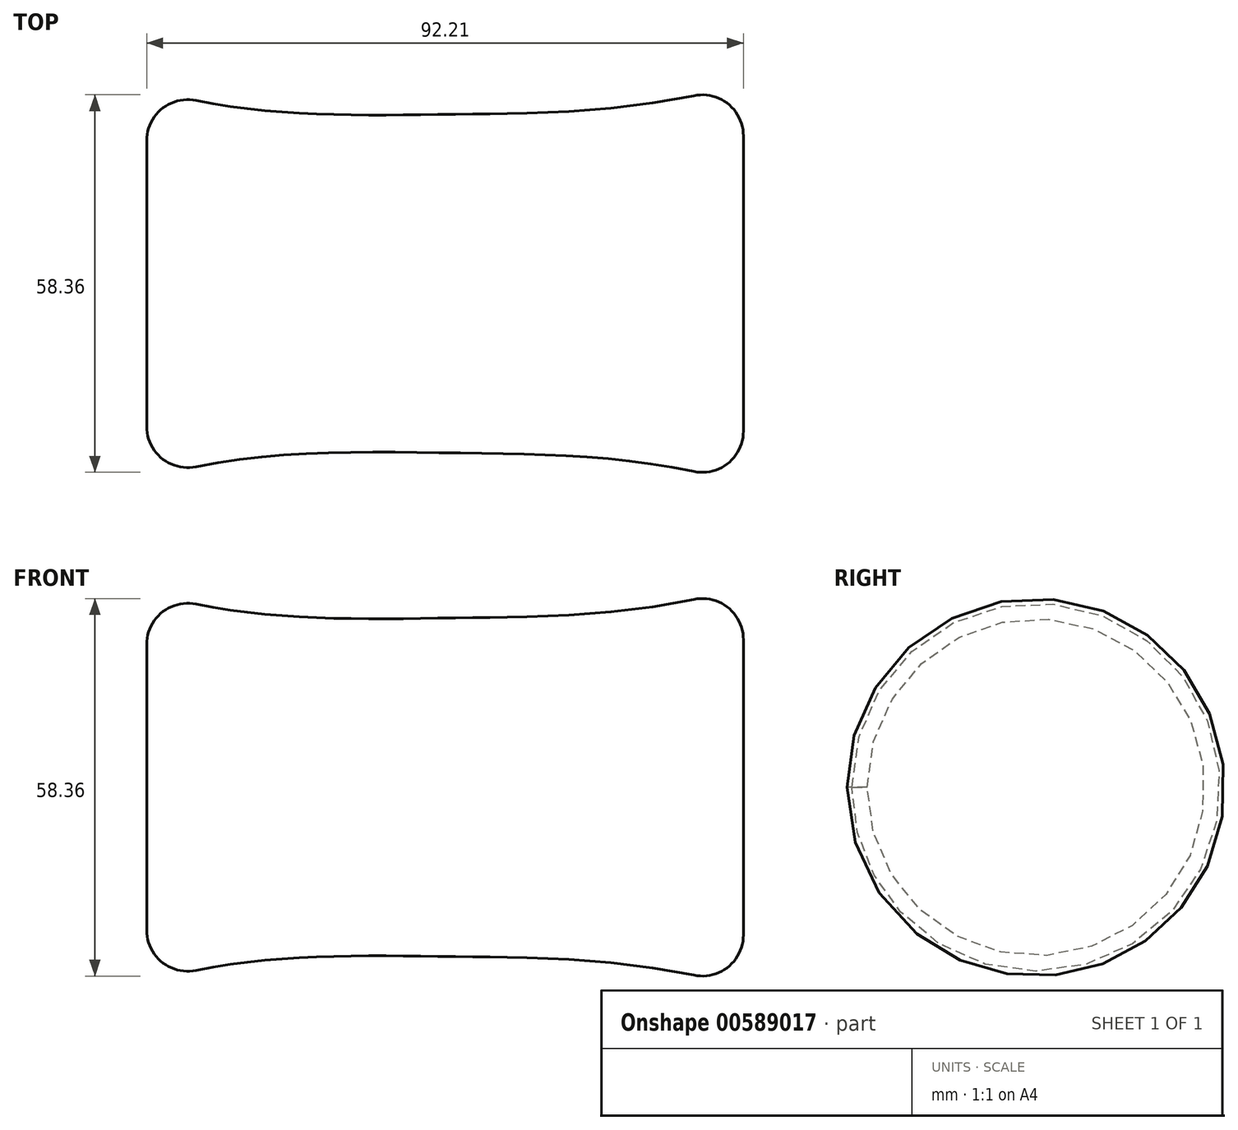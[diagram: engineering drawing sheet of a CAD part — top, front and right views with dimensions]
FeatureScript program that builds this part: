
annotation { "Feature Type Name" : "Feature", "Feature Type Description" : "" }
export const myFeature = defineFeature(function(context is Context, id is Id, definition is map)
    precondition{}
    {
        {
            var Q0;
            Q0=qCreatedBy(makeId("Top.planeOp"),FACE);
            var sketch = newSketch(context, id + "F0", { "sketchPlane" : qUnion([Q0])});
            skFitSpline(sketch, "E0", {"points": [v(-47.17, 38.3) * mm, v(0, 34.19) * mm, v(45.04, 38.97) * mm], "startDerivative": vector(89.11, -28.28) * mm, "endDerivative": vector(96.4, 27.82) * mm});
            skLineSegment(sketch, "E1", {"start": v(-47.17, 30.1) * mm, "end": v(-47.17, 8.02) * mm});
            skLineSegment(sketch, "E2", {"start": v(-47.17, 8.02) * mm, "end": v(45.04, 8.02) * mm});
            skLineSegment(sketch, "E3", {"start": v(45.04, 8.02) * mm, "end": v(45.04, 30.85) * mm});
            skArc(sketch, "E4.filletArc", {"start": v(-39.55, 36.33) * mm, "mid": v(-44.84, 35.03) * mm, "end": v(-47.17, 30.1) * mm});
            skArc(sketch, "E5.filletArc", {"start": v(45.04, 30.85) * mm, "mid": v(42.7, 35.78) * mm, "end": v(37.39, 37.07) * mm});
            skSolve(sketch);
        }
        {
            var Q0;
            Q0=makeQuery(id+"F0.imprint","IMPRINT",FACE,{"disambiguationData":[TD([[makeQuery(id+"F0.imprint","IMPRINT",EDGE,{"derivedFrom":sQuery(id+"F0.wireOp",EDGE,"E0")}),-1.0]])]});
            var Q1;
            Q1=sQuery(id+"F0.wireOp",EDGE,"E2");
            revolve(context, id + "F1", {"entities" : qUnion([Q0]), "axis" : qUnion([Q1]), "revolveType" : RevolveType.FULL});
        }
    });
